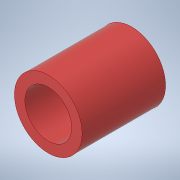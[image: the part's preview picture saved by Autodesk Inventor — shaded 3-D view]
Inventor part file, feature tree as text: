
AUTODESK INVENTOR PART (.ipt)
format: ipt  version: 2022.3 (Build 263350000, 350)  size: 107,520 bytes
history: native  units: in
note: dims shown in document units (in); Inventor stores cm internally (conversion verified against a paired STEP export)
features: sketch x1, extrude x1
ambient origin geometry x8: Origin, YZ Plane, XZ Plane, XY Plane, X Axis, Y Axis, Z Axis, Center Point
bodies: Solid1 (feature_tree)
feature tree (2):
  sketch  "Sketch1"  dims[d1=1.0in d2=0.0in d13=0.561in d14=0.125in]
  extrude  "Extrusion1"  TaperAngle=0.0deg  [1 undecoded]
note: 1 required parameter value undecoded (feature->parameter linkage not recoverable at this tier; creation-order binding heuristic only, values carry confidence <= 0.55)
